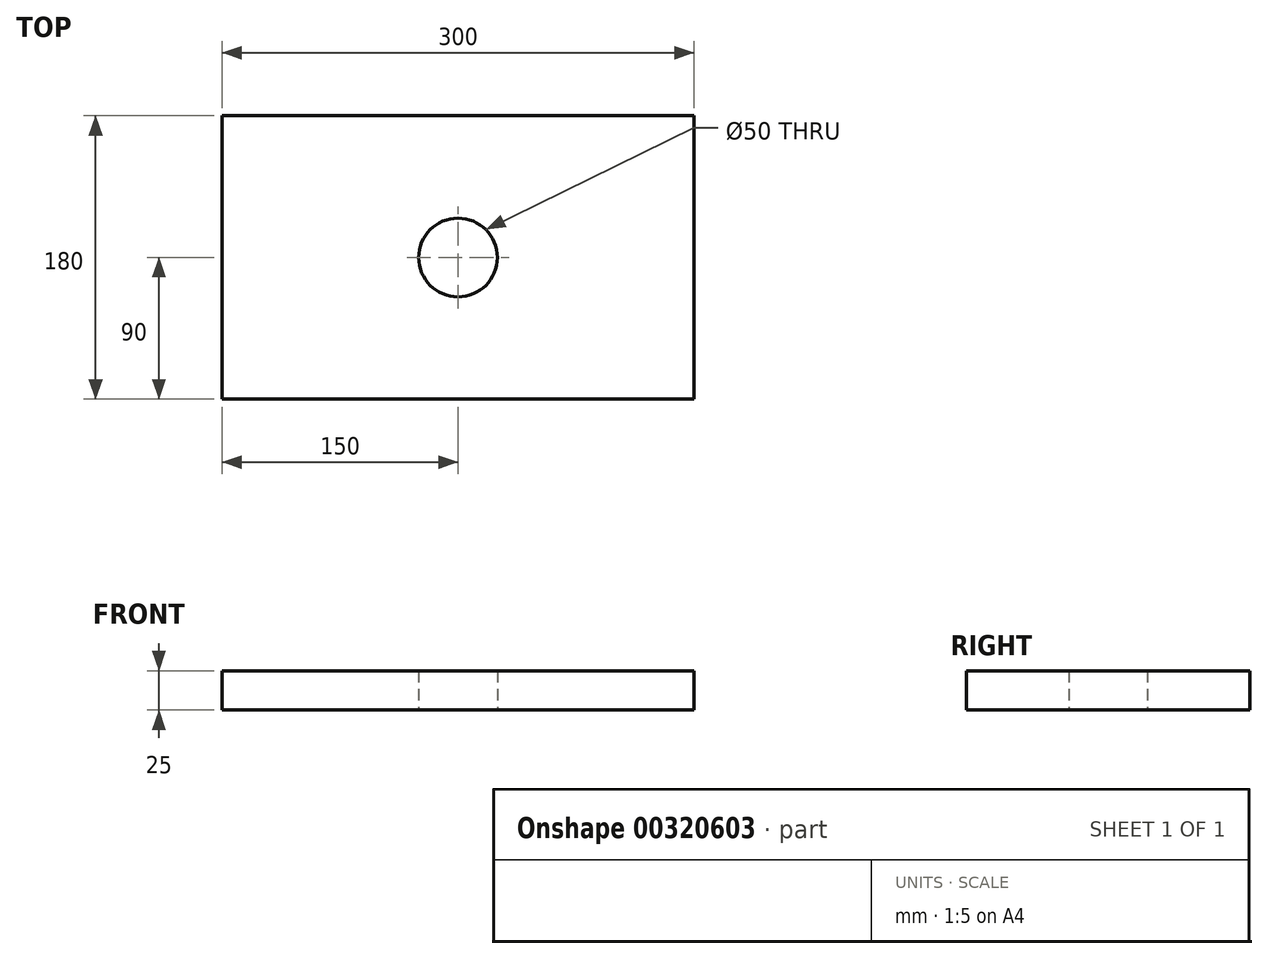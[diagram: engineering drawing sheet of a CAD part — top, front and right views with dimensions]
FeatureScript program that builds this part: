
annotation { "Feature Type Name" : "Feature", "Feature Type Description" : "" }
export const myFeature = defineFeature(function(context is Context, id is Id, definition is map)
    precondition{}
    {
        {
            var Q0;
            Q0=qCreatedBy(makeId("Top.planeOp"),FACE);
            var sketch = newSketch(context, id + "F0", { "sketchPlane" : qUnion([Q0])});
            skLineSegment(sketch, "E0.bottom", {"start": v(150, 90) * mm, "end": v(-150, 90) * mm});
            skLineSegment(sketch, "E0.top", {"start": v(150, -90) * mm, "end": v(-150, -90) * mm});
            skLineSegment(sketch, "E0.left", {"start": v(150, 90) * mm, "end": v(150, -90) * mm});
            skLineSegment(sketch, "E0.right", {"start": v(-150, 90) * mm, "end": v(-150, -90) * mm});
            skPoint(sketch, "E0.middle", {"position": v(0, 0) * mm});
            skCircle(sketch, "E1", {"center": v(0, 0) * mm, "radius": 24 * mm});
            skCircle(sketch, "E2", {"center": v(0, 0) * mm, "radius": 25 * mm});
            skSolve(sketch);
        }
        {
            var Q0;
            Q0=makeQuery(id+"F0.imprint","IMPRINT",FACE,{"disambiguationData":[TD([[makeQuery(id+"F0.imprint","IMPRINT",EDGE,{"derivedFrom":sQuery(id+"F0.wireOp",EDGE,"E0.bottom")}),1.0]])]});
            extrude(context, id + "F1", {"entities" : qUnion([Q0]), "depth" : 5 * mm});
        }
        {
            var Q0;
            Q0=makeQuery(id+"F0.imprint","IMPRINT",FACE,{"disambiguationData":[TD([[makeQuery(id+"F0.imprint","IMPRINT",EDGE,{"derivedFrom":sQuery(id+"F0.wireOp",EDGE,"E0.bottom")}),1.0]])]});
            extrude(context, id + "F2", {"entities" : qUnion([Q0]), "operationType" : NewBodyOperationType.ADD, "depth" : 25 * mm});
        }
    });
